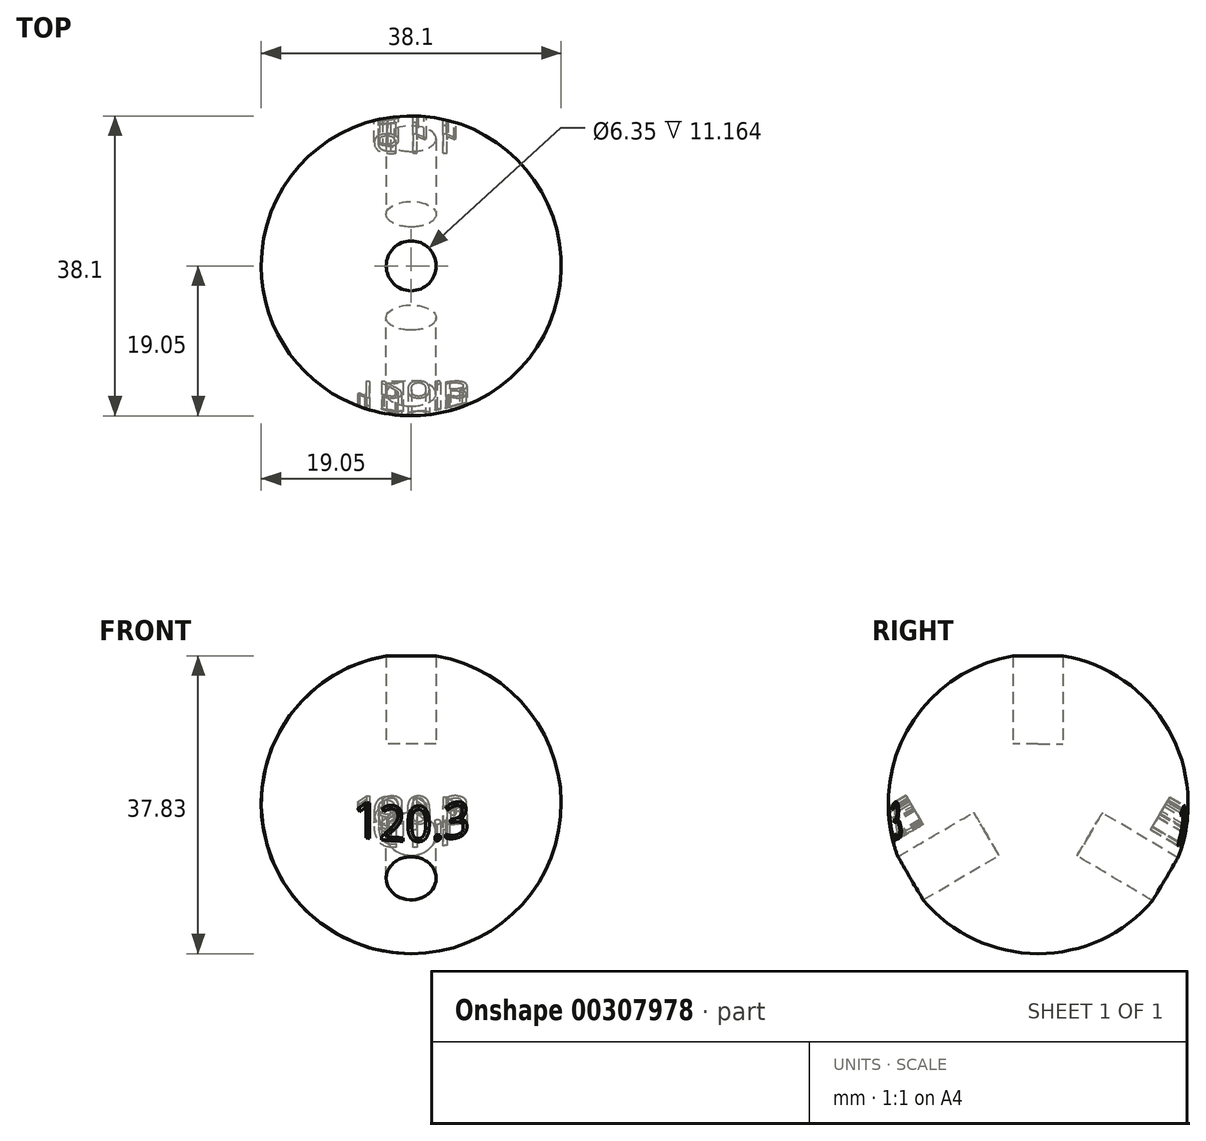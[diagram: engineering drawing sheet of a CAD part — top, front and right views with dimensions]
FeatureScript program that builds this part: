
annotation { "Feature Type Name" : "Feature", "Feature Type Description" : "" }
export const myFeature = defineFeature(function(context is Context, id is Id, definition is map)
    precondition{}
    {
        {
            var Q0;
            Q0=qCreatedBy(makeId("Front.planeOp"),FACE);
            var sketch = newSketch(context, id + "F0", { "sketchPlane" : qUnion([Q0])});
            skArc(sketch, "E0", {"start": v(0, 19.05) * mm, "mid": v(-19.05, 0) * mm, "end": v(0, -19.05) * mm});
            skLineSegment(sketch, "E1", {"start": v(0, 19.05) * mm, "end": v(0, -19.05) * mm});
            skSolve(sketch);
        }
        {
            var Q0;
            Q0=qCreatedBy(makeId("Top.planeOp"),FACE);
            var sketch = newSketch(context, id + "F1", { "sketchPlane" : qUnion([Q0])});
            skCircle(sketch, "E2", {"center": v(0, 0) * mm, "radius": 19.05 * mm});
            skSolve(sketch);
        }
        {
            var Q0;
            Q0=makeQuery(id+"F0.imprint","IMPRINT",FACE,{"disambiguationData":[TD([[makeQuery(id+"F0.imprint","IMPRINT",EDGE,{"derivedFrom":sQuery(id+"F0.wireOp",EDGE,"E0")}),1.0]])]});
            var Q1;
            Q1=sQuery(id+"F1.wireOp",EDGE,"E2");
            revolve(context, id + "F2", {"entities" : qUnion([Q0]), "axis" : qUnion([Q1]), "revolveType" : RevolveType.FULL});
        }
        {
            var Q0;
            Q0=qCreatedBy(makeId("Front.planeOp"),FACE);
            var sketch = newSketch(context, id + "F3", { "sketchPlane" : qUnion([Q0])});
            skLineSegment(sketch, "E3", {"start": v(0, 0) * mm, "end": v(76.32, 0) * mm, "construction": true});
            skLineSegment(sketch, "E4", {"start": v(0, 0) * mm, "end": v(0, 76.7) * mm, "construction": true});
            skSolve(sketch);
        }
        {
            var Q0;
            Q0=qCreatedBy(makeId("Top.planeOp"),FACE);
            cPlane(context, id + "F4", {"entities" : qUnion([Q0]), "cplaneType" : CPlaneType.OFFSET, "offset" : 7.62 * mm, "width" : 152.4 * mm, "height" : 152.4 * mm});
        }
        {
            var Q0;
            Q0=qCreatedBy(id+"F4.planeOp",FACE);
            var sketch = newSketch(context, id + "F5", { "sketchPlane" : qUnion([Q0])});
            skCircle(sketch, "E5", {"center": v(0, 0) * mm, "radius": 3.17 * mm});
            skSolve(sketch);
        }
        {
            var Q0;
            Q0=qSketchRegion(id+"F5",true);
            extrude(context, id + "F6", {"entities" : qUnion([Q0]), "depth" : 76.2 * mm});
        }
        {
            var Q0;
            Q0=makeQuery(id+"F6.opExtrude","SWEPT_BODY",BODY,{"disambiguationData":[OSD([sQuery(id+"F5.wireOp",EDGE,"E5")])]});
            var Q1;
            Q1=sQuery(id+"F3.wireOp",EDGE,"E3");
            transform(context, id + "F7", {"entities" : qUnion([Q0]), "transformType" : TransformType.ROTATION, "transformAxis" : qUnion([Q1]), "angle" : 120.3 * degree, "makeCopy" : true});
        }
        {
            var Q0;
            Q0=makeQuery(id+"F7.opPattern","COPY",BODY,{"derivedFrom":makeQuery(id+"F6.opExtrude","SWEPT_BODY",BODY,{"disambiguationData":[OSD([sQuery(id+"F5.wireOp",EDGE,"E5")])]}),"instanceName":"1"});
            var Q1;
            Q1=sQuery(id+"F3.wireOp",EDGE,"E3");
            transform(context, id + "F8", {"entities" : qUnion([Q0]), "transformType" : TransformType.ROTATION, "transformAxis" : qUnion([Q1]), "angle" : 119 * degree, "makeCopy" : true});
        }
        {
            var Q0;
            Q0=makeQuery(id+"F7.opPattern","COPY",FACE,{"derivedFrom":makeQuery(id+"F6.opExtrude","CAP_FACE",FACE,{"disambiguationData":[OSD([sQuery(id+"F5.wireOp",EDGE,"E5")])],"isStart":false}),"instanceName":"1"});
            cPlane(context, id + "F9", {"entities" : qUnion([Q0]), "cplaneType" : CPlaneType.OFFSET, "offset" : 63.5 * mm, "oppositeDirection" : true, "width" : 152.4 * mm, "height" : 152.4 * mm});
        }
        {
            var Q0;
            Q0=qCreatedBy(id+"F9.planeOp",FACE);
            var sketch = newSketch(context, id + "F10", { "sketchPlane" : qUnion([Q0])});
            skText(sketch, "E6", { "text": "120.3", "fontName": "OpenSans-Regular.ttf"});
            const initialGuessF10  = {"E6": [-0.00732, 0.00517, 1, 0, 0.00416]};
            skSetInitialGuess(sketch, initialGuessF10);
            skSolve(sketch);
        }
        {
            var Q0;
            Q0=qSketchRegion(id+"F10",true);
            extrude(context, id + "F11", {"entities" : qUnion([Q0]), "operationType" : NewBodyOperationType.REMOVE, "oppositeDirection" : true, "depth" : 6.35 * mm});
        }
        {
            var Q0;
            Q0=makeQuery(id+"F8.opPattern","COPY",FACE,{"derivedFrom":makeQuery(id+"F7.opPattern","COPY",FACE,{"derivedFrom":makeQuery(id+"F6.opExtrude","CAP_FACE",FACE,{"disambiguationData":[OSD([sQuery(id+"F5.wireOp",EDGE,"E5")])],"isStart":false}),"instanceName":"1"}),"instanceName":"1"});
            cPlane(context, id + "F12", {"entities" : qUnion([Q0]), "cplaneType" : CPlaneType.OFFSET, "offset" : 63.5 * mm, "oppositeDirection" : true, "width" : 152.4 * mm, "height" : 152.4 * mm});
        }
        {
            var Q0;
            Q0=qCreatedBy(id+"F12.planeOp",FACE);
            var sketch = newSketch(context, id + "F13", { "sketchPlane" : qUnion([Q0])});
            skText(sketch, "E7", { "text": "119", "fontName": "OpenSans-Regular.ttf"});
            const initialGuessF13  = {"E7": [-0.00634, 0.0045, 1, 0, 0.00478]};
            skSetInitialGuess(sketch, initialGuessF13);
            skSolve(sketch);
        }
        {
            var Q0;
            Q0=qSketchRegion(id+"F13",true);
            extrude(context, id + "F14", {"entities" : qUnion([Q0]), "operationType" : NewBodyOperationType.REMOVE, "oppositeDirection" : true, "depth" : 6.35 * mm});
        }
        {
            var Q0;
            Q0=makeQuery(id+"F6.opExtrude","SWEPT_BODY",BODY,{"disambiguationData":[OSD([sQuery(id+"F5.wireOp",EDGE,"E5")])]});
            var Q1;
            Q1=makeQuery(id+"F7.opPattern","COPY",BODY,{"derivedFrom":makeQuery(id+"F6.opExtrude","SWEPT_BODY",BODY,{"disambiguationData":[OSD([sQuery(id+"F5.wireOp",EDGE,"E5")])]}),"instanceName":"1"});
            var Q2;
            Q2=makeQuery(id+"F8.opPattern","COPY",BODY,{"derivedFrom":makeQuery(id+"F7.opPattern","COPY",BODY,{"derivedFrom":makeQuery(id+"F6.opExtrude","SWEPT_BODY",BODY,{"disambiguationData":[OSD([sQuery(id+"F5.wireOp",EDGE,"E5")])]}),"instanceName":"1"}),"instanceName":"1"});
            var Q3;
            Q3=makeQuery(id+"F2.opRevolve","SWEPT_BODY",BODY,{"disambiguationData":[OSD([sQuery(id+"F0.wireOp",EDGE,"E0"),sQuery(id+"F0.wireOp",EDGE,"E1")])]});
            booleanBodies(context, id + "F15", {"operationType" : BooleanOperationType.SUBTRACTION, "tools" : qUnion([Q0, Q1, Q2]), "targets" : qUnion([Q3])});
        }
    });
